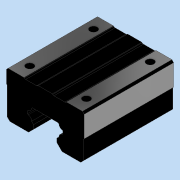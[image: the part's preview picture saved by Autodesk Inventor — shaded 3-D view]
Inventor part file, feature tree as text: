
AUTODESK INVENTOR PART (.ipt)
format: ipt  version: 2021 (Build 250183000, 183)  size: 186,368 bytes
history: native  units: mm
features: extrude x2, sketch x2, projected_geometry x2
ambient origin geometry x8: Origin, YZ Plane, XZ Plane, XY Plane, X Axis, Y Axis, Z Axis, Center Point
bodies: Solid1 (feature_tree)
feature tree (6):
  extrude  "Extrusion1"  Depth=6.0mm TaperAngle=0.0deg
  extrude  "Extrusion2"  [1 undecoded]
  sketch  "Sketch1"  dims[d0=50.5mm d1=0.0mm d2=6.0mm d3=0.0mm]
  sketch  "Sketch3"
  projected_geometry  "Projected Loop1"
  projected_geometry  "Projected Loop2"
note: 1 required parameter value undecoded (feature->parameter linkage not recoverable at this tier; creation-order binding heuristic only, values carry confidence <= 0.55)
